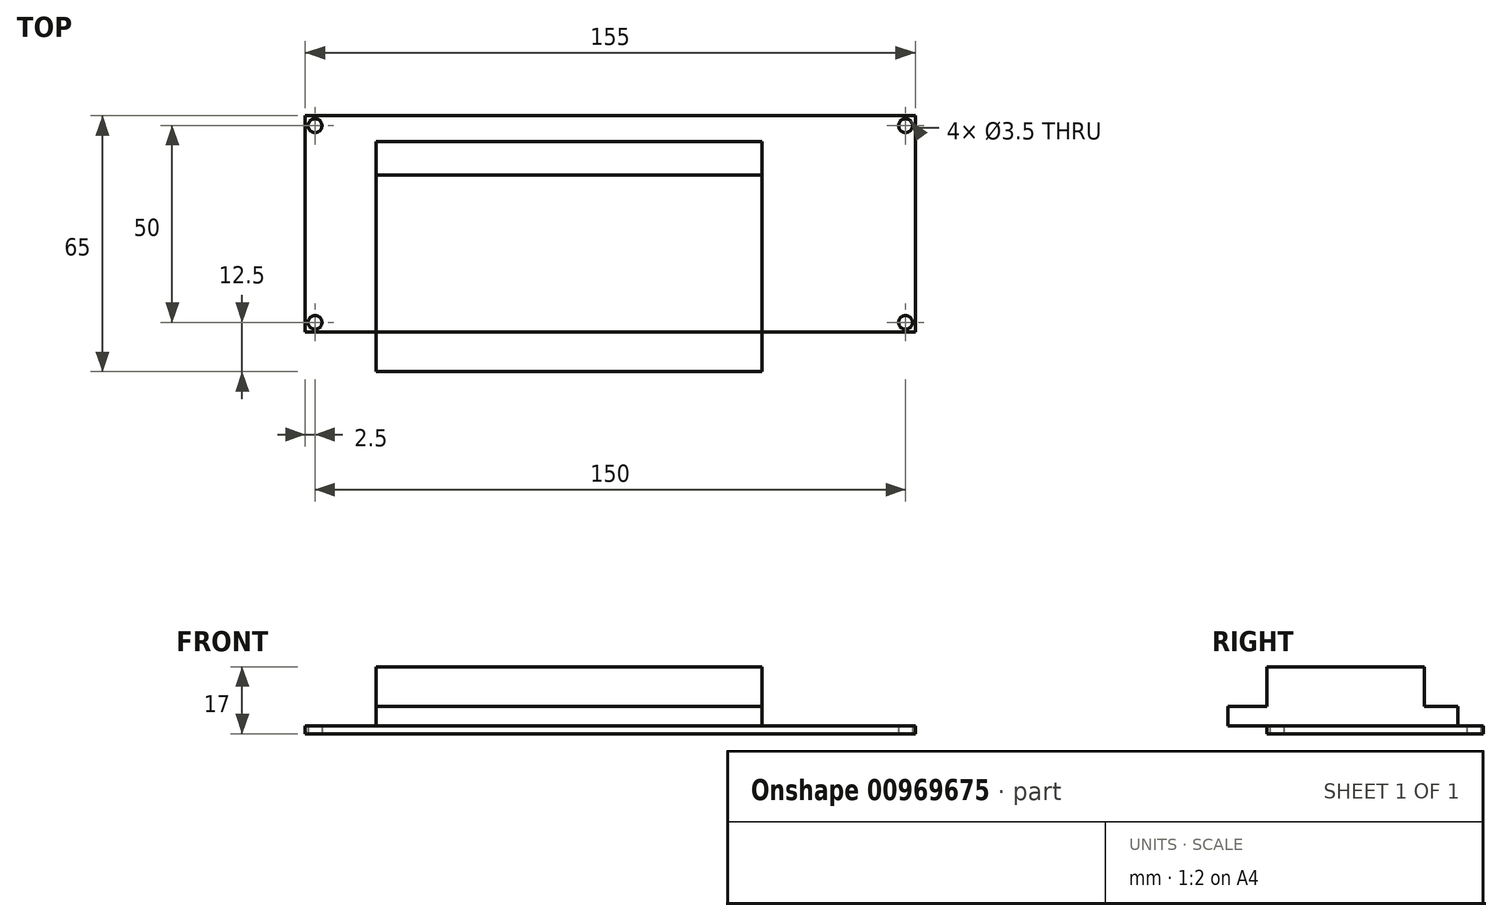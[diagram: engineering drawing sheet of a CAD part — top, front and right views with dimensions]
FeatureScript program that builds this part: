
annotation { "Feature Type Name" : "Feature", "Feature Type Description" : "" }
export const myFeature = defineFeature(function(context is Context, id is Id, definition is map)
    precondition{}
    {
        {
            var Q0;
            Q0=qCreatedBy(makeId("Top.planeOp"),FACE);
            var sketch = newSketch(context, id + "F0", { "sketchPlane" : qUnion([Q0])});
            skLineSegment(sketch, "E0.bottom", {"start": v(-77.5, 27.5) * mm, "end": v(77.5, 27.5) * mm});
            skLineSegment(sketch, "E0.top", {"start": v(-77.5, -27.5) * mm, "end": v(77.5, -27.5) * mm});
            skLineSegment(sketch, "E0.left", {"start": v(-77.5, 27.5) * mm, "end": v(-77.5, -27.5) * mm});
            skLineSegment(sketch, "E0.right", {"start": v(77.5, 27.5) * mm, "end": v(77.5, -27.5) * mm});
            skLineSegment(sketch, "E1", {"start": v(-77.5, 0) * mm, "end": v(0, 0) * mm, "construction": true});
            skLineSegment(sketch, "E2", {"start": v(0, 0) * mm, "end": v(0, 27.5) * mm, "construction": true});
            skCircle(sketch, "E3", {"center": v(-75, 25) * mm, "radius": 1.75 * mm});
            skCircle(sketch, "E4", {"center": v(-75, -25) * mm, "radius": 1.75 * mm});
            skCircle(sketch, "E5", {"center": v(75, -25) * mm, "radius": 1.75 * mm});
            skCircle(sketch, "E6", {"center": v(75, 25) * mm, "radius": 1.75 * mm});
            skLineSegment(sketch, "E7.bottom", {"start": v(-75, 25) * mm, "end": v(75, 25) * mm, "construction": true});
            skLineSegment(sketch, "E7.top", {"start": v(-75, -25) * mm, "end": v(75, -25) * mm, "construction": true});
            skLineSegment(sketch, "E7.left", {"start": v(-75, 25) * mm, "end": v(-75, -25) * mm, "construction": true});
            skLineSegment(sketch, "E7.right", {"start": v(75, 25) * mm, "end": v(75, -25) * mm, "construction": true});
            skSolve(sketch);
        }
        {
            var Q0;
            Q0 = qSketchRegion(id + "F0", true);
            extrude(context, id + "F1", {"entities" : qUnion([Q0]), "depth" : 2 * mm, "offsetDistance" : 25 * mm});
        }
        {
            var Q0;
            Q0=makeQuery(id+"F1.opExtrude","CAP_FACE",FACE,{"disambiguationData":[OSD([sQuery(id+"F0.wireOp",EDGE,"E0.bottom"),sQuery(id+"F0.wireOp",EDGE,"E0.top"),sQuery(id+"F0.wireOp",EDGE,"E0.left"),sQuery(id+"F0.wireOp",EDGE,"E0.right"),sQuery(id+"F0.wireOp",EDGE,"E3"),sQuery(id+"F0.wireOp",EDGE,"E4"),sQuery(id+"F0.wireOp",EDGE,"E5"),sQuery(id+"F0.wireOp",EDGE,"E6")])],"isStart":false});
            var sketch = newSketch(context, id + "F2", { "sketchPlane" : qUnion([Q0])});
            skLineSegment(sketch, "E8.bottom", {"start": v(-59.5, 21.01) * mm, "end": v(38.5, 21.01) * mm});
            skLineSegment(sketch, "E8.top", {"start": v(-59.5, -37.5) * mm, "end": v(38.5, -37.5) * mm});
            skLineSegment(sketch, "E8.left", {"start": v(-59.5, 21.01) * mm, "end": v(-59.5, -37.5) * mm});
            skLineSegment(sketch, "E8.right", {"start": v(38.5, 21.01) * mm, "end": v(38.5, -37.5) * mm});
            skSolve(sketch);
        }
        {
            var Q0;
            {var subQ0=sQuery(id+"F2.wireOp",EDGE,"E8.bottom");Q0=makeQuery(id+"F2.imprint","IMPRINT",FACE,{"disambiguationData":[TD([[makeQuery(id+"F2.imprint","IMPRINT",EDGE,{"derivedFrom":subQ0}),-1.0]])]});}
            var Q1;
            {var subQ0=sQuery(id+"F2.wireOp",EDGE,"E8.top");Q1=makeQuery(id+"F2.imprint","IMPRINT",FACE,{"disambiguationData":[TD([[makeQuery(id+"F2.imprint","IMPRINT",EDGE,{"derivedFrom":subQ0}),1.0]])]});}
            extrude(context, id + "F3", {"entities" : qUnion([Q0, Q1]), "operationType" : NewBodyOperationType.ADD, "depth" : 5 * mm, "offsetDistance" : 25 * mm});
        }
        {
            var Q0;
            Q0=makeQuery(id+"F3.opExtrude","CAP_FACE",FACE,{"disambiguationData":[OSD([sQuery(id+"F2.wireOp",EDGE,"E8.bottom"),sQuery(id+"F2.wireOp",EDGE,"E8.top"),sQuery(id+"F2.wireOp",EDGE,"E8.left"),sQuery(id+"F2.wireOp",EDGE,"E8.right")])],"isStart":false});
            var sketch = newSketch(context, id + "F4", { "sketchPlane" : qUnion([Q0])});
            skLineSegment(sketch, "E9.bottom", {"start": v(-59.5, 12.5) * mm, "end": v(38.5, 12.5) * mm});
            skLineSegment(sketch, "E9.top", {"start": v(-59.5, -27.5) * mm, "end": v(38.5, -27.5) * mm});
            skLineSegment(sketch, "E9.left", {"start": v(-59.5, 12.5) * mm, "end": v(-59.5, -27.5) * mm});
            skLineSegment(sketch, "E9.right", {"start": v(38.5, 12.5) * mm, "end": v(38.5, -27.5) * mm});
            skSolve(sketch);
        }
        {
            var Q0;
            Q0 = qSketchRegion(id + "F4", true);
            extrude(context, id + "F5", {"entities" : qUnion([Q0]), "operationType" : NewBodyOperationType.ADD, "depth" : 10 * mm, "offsetDistance" : 25 * mm});
        }
    });
